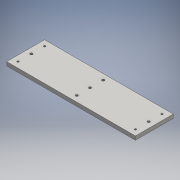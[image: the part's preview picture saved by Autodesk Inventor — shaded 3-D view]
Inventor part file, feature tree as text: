
AUTODESK INVENTOR PART (.ipt)
format: ipt  version: 2016 (Build 200138000, 138)  size: 125,952 bytes
history: native  units: mm
features: sketch x3, hole x2, mirror x2, extrude x1
ambient origin geometry x8: Origin, YZ Plane, XZ Plane, XY Plane, X Axis, Y Axis, Z Axis, Center Point
bodies: Solid1 (feature_tree)
feature tree (8):
  extrude  "baseExtrusion"  Depth=340.0mm
  hole  "xyStiltpt1m6MountingHoles"  [1 undecoded]
  mirror  "Mirror2"
  mirror  "Mirror3"
  hole  "Hole3"  [1 undecoded]
  sketch  "Sketch1"  dims[d0=340.0mm d1=170.0mm]
  sketch  "Sketch2"  dims[d2=100.0mm d3=50.0mm]
  sketch  "Sketch4"  dims[d4=10.0mm d5=0.0mm d6=15.0mm d7=15.0mm d8=4.917mm d9=12.0mm d10=4.0mm d11=2.0mm d12=90.0deg d13=17.1mm d14=20.594885mm d24=15.0mm d25=15.0mm d26=15.0mm d27=15.0mm d28=6.6mm d29=12.0mm d30=18.0mm d31=4.8mm d32=90.0deg d33=17.1mm d34=20.594885mm]
note: 2 required parameter values undecoded (feature->parameter linkage not recoverable at this tier; creation-order binding heuristic only, values carry confidence <= 0.55)
